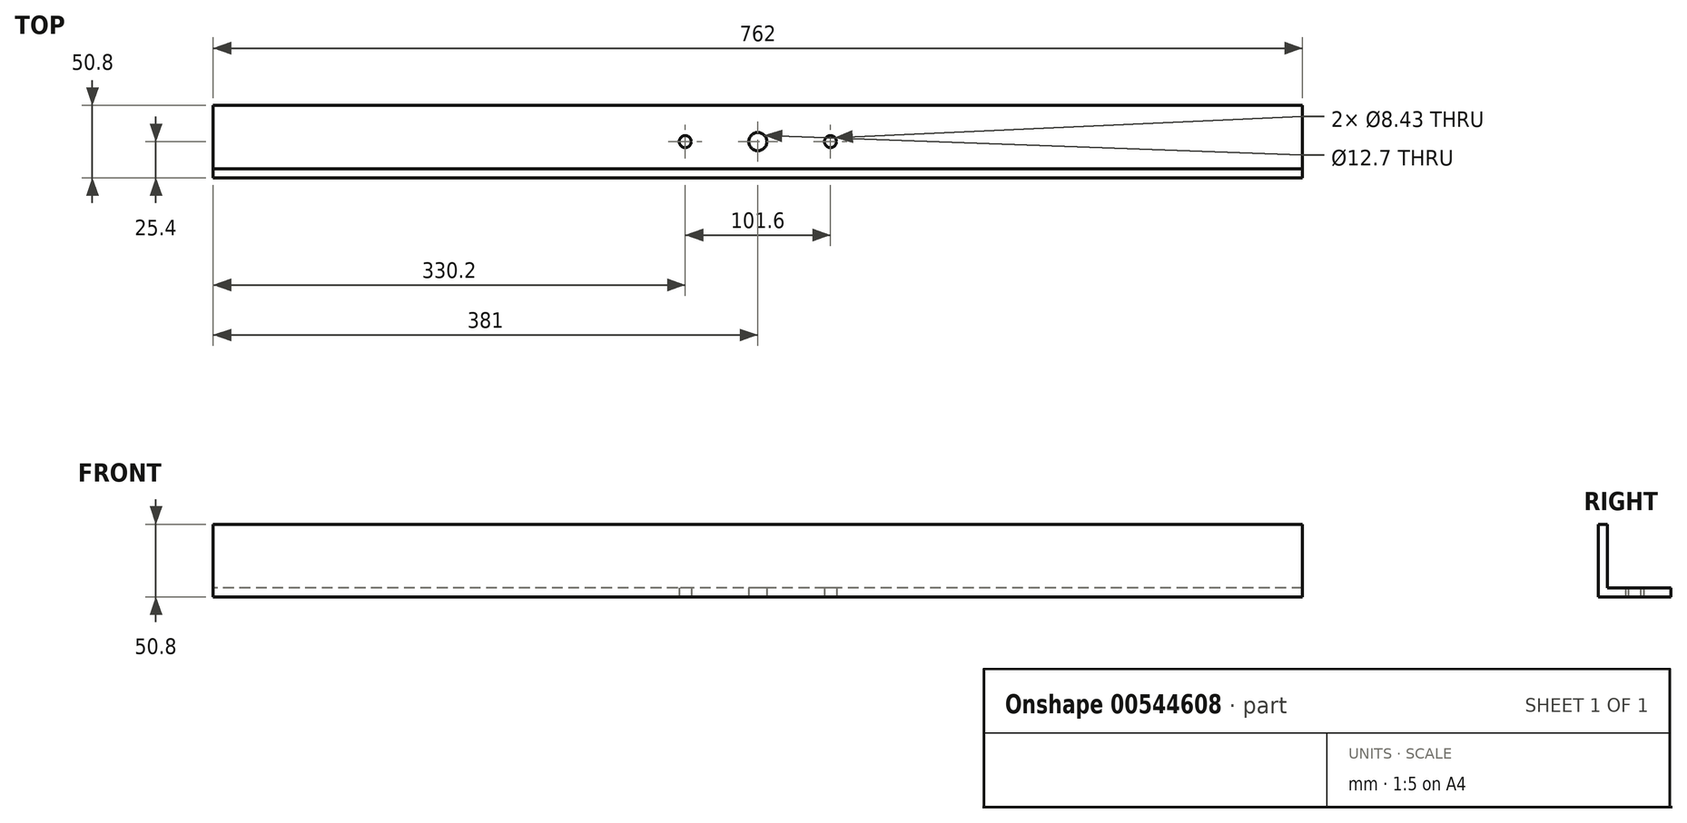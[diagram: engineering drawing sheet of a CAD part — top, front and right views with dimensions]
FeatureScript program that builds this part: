
annotation { "Feature Type Name" : "Feature", "Feature Type Description" : "" }
export const myFeature = defineFeature(function(context is Context, id is Id, definition is map)
    precondition{}
    {
        {
            var Q0;
            Q0=qCreatedBy(makeId("Right.planeOp"),FACE);
            var sketch = newSketch(context, id + "F0", { "sketchPlane" : qUnion([Q0])});
            skLineSegment(sketch, "E0.bottom", {"start": v(0, 0) * mm, "end": v(50.8, 0) * mm});
            skLineSegment(sketch, "E0.top", {"start": v(0, 50.8) * mm, "end": v(6.35, 50.8) * mm});
            skLineSegment(sketch, "E0.left", {"start": v(0, 0) * mm, "end": v(0, 50.8) * mm});
            skLineSegment(sketch, "E0.right", {"start": v(50.8, 0) * mm, "end": v(50.8, 6.35) * mm});
            skLineSegment(sketch, "E1.0", {"start": v(6.35, 6.35) * mm, "end": v(6.35, 50.8) * mm});
            skLineSegment(sketch, "E1.1", {"start": v(6.35, 6.35) * mm, "end": v(50.8, 6.35) * mm});
            skSolve(sketch);
        }
        {
            var Q0;
            Q0=makeQuery(id+"F0.imprint","IMPRINT",FACE,{"disambiguationData":[TD([[makeQuery(id+"F0.imprint","IMPRINT",EDGE,{"derivedFrom":sQuery(id+"F0.wireOp",EDGE,"E0.bottom")}),1.0]])]});
            extrude(context, id + "F1", {"entities" : qUnion([Q0]), "endBound" : BoundingType.SYMMETRIC, "depth" : 762 * mm, "offsetDistance" : 25.4 * mm});
        }
        {
            var Q0;
            Q0=makeQuery(id+"F1.opExtrude","SWEPT_FACE",FACE,{"disambiguationData":[OSD([sQuery(id+"F0.wireOp",EDGE,"E0.bottom")])]});
            var sketch = newSketch(context, id + "F2", { "sketchPlane" : qUnion([Q0])});
            skCircle(sketch, "E2", {"center": v(0, -25.4) * mm, "radius": 6.35 * mm});
            skSolve(sketch);
        }
        {
            var Q0;
            Q0=makeQuery(id+"F2.imprint","IMPRINT",FACE,{"disambiguationData":[TD([[makeQuery(id+"F2.imprint","IMPRINT",EDGE,{"derivedFrom":sQuery(id+"F2.wireOp",EDGE,"E2")}),1.0]])]});
            extrude(context, id + "F3", {"entities" : qUnion([Q0]), "operationType" : NewBodyOperationType.REMOVE, "endBound" : BoundingType.THROUGH_ALL, "oppositeDirection" : true, "depth" : 25.4 * mm, "offsetDistance" : 25.4 * mm});
        }
        {
            var Q0;
            Q0=makeQuery(id+"F1.opExtrude","SWEPT_FACE",FACE,{"disambiguationData":[OSD([sQuery(id+"F0.wireOp",EDGE,"E0.bottom")])]});
            var sketch = newSketch(context, id + "F4", { "sketchPlane" : qUnion([Q0])});
            skPoint(sketch, "E3", {"position": v(50.8, -25.4) * mm});
            skPoint(sketch, "E4", {"position": v(-50.8, -25.4) * mm});
            skCircle(sketch, "E5.0", {"center": v(0, -25.4) * mm, "radius": 6.35 * mm, "construction": true});
            skSolve(sketch);
        }
        {
            var Q0;
            Q0=sQuery(id+"F4.wireOp",VERTEX,"E3");
            var Q1;
            Q1=sQuery(id+"F4.wireOp",VERTEX,"E4");
            var Q2;
            Q2=makeQuery(id+"F1.opExtrude","SWEPT_BODY",BODY,{"disambiguationData":[OSD([sQuery(id+"F0.wireOp",EDGE,"E0.bottom"),sQuery(id+"F0.wireOp",EDGE,"E0.top"),sQuery(id+"F0.wireOp",EDGE,"E0.left"),sQuery(id+"F0.wireOp",EDGE,"E0.right"),sQuery(id+"F0.wireOp",EDGE,"E1.0"),sQuery(id+"F0.wireOp",EDGE,"E1.1")])]});
            hole(context, id + "F5", {"style" : HoleStyle.SIMPLE, "endStyle" : HoleEndStyle.THROUGH, "standardTappedOrClearance" : lookupTablePath({ "fit" : "Normal (ASME)", "standard" : "ANSI", "size" : "5/16", "type" : "Clearance" }), "standardBlindInLast" : lookupTablePath({ "fit" : "Free", "standard" : "ANSI", "size" : "5/16", "type" : "Clearance" }), "holeDiameter" : 8.43 * mm, "isTappedThrough" : true, "tappedDepth" : 12.7 * mm, "tapClearance" : 3, "locations" : qUnion([Q0, Q1]), "scope" : qUnion([Q2])});
        }
    });
